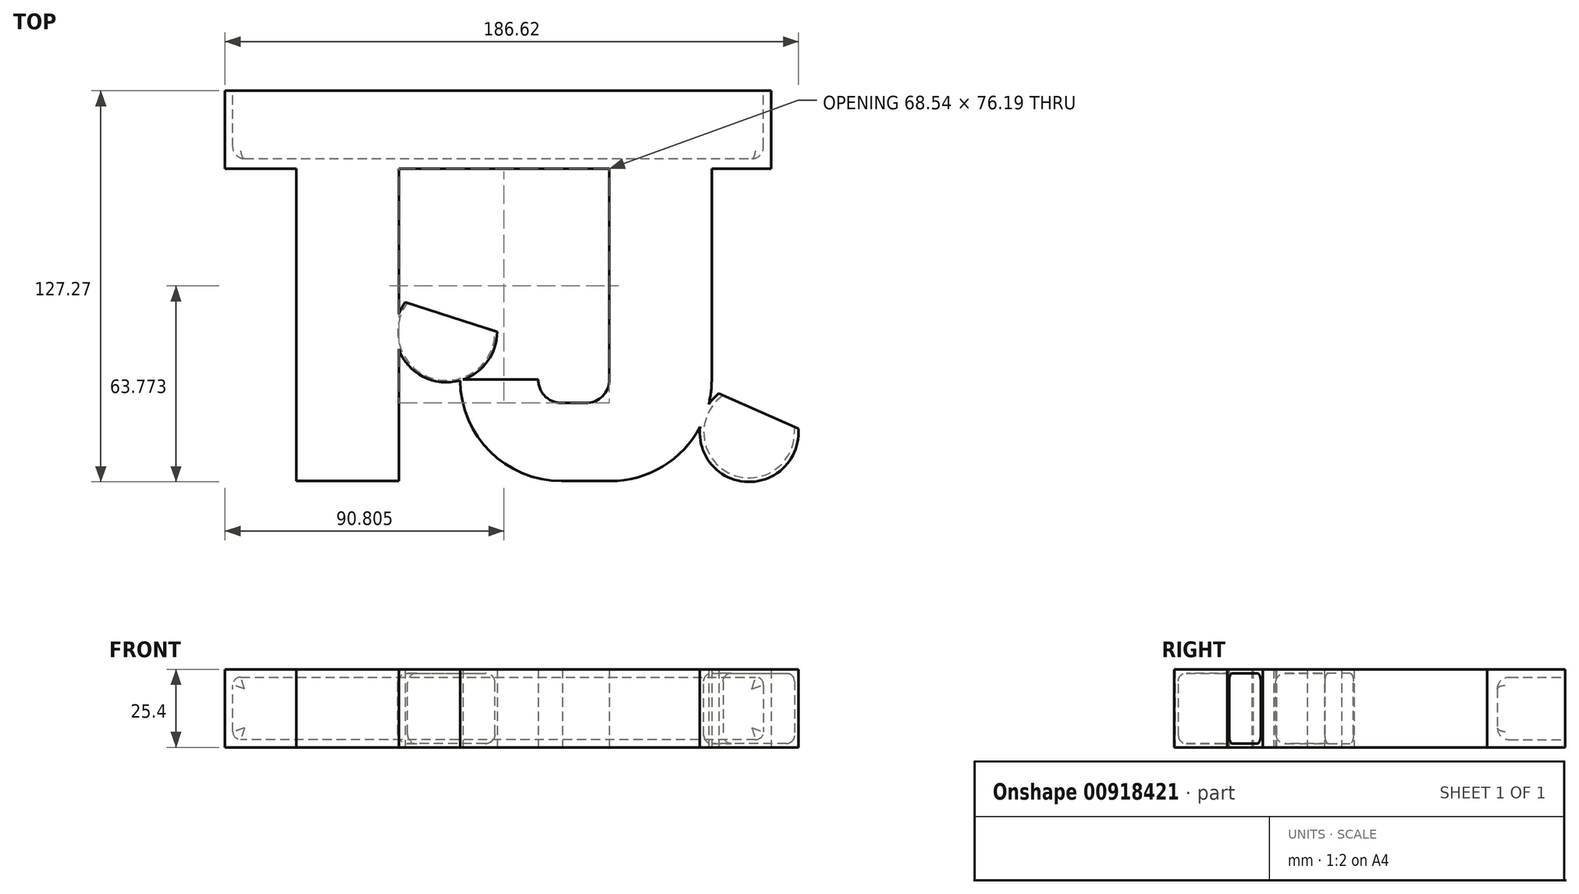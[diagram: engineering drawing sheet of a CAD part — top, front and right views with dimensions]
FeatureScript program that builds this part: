
annotation { "Feature Type Name" : "Feature", "Feature Type Description" : "" }
export const myFeature = defineFeature(function(context is Context, id is Id, definition is map)
    precondition{}
    {
        {
            var Q0;
            Q0=qCreatedBy(makeId("Top.planeOp"),FACE);
            var sketch = newSketch(context, id + "F0", { "sketchPlane" : qUnion([Q0])});
            skLineSegment(sketch, "E0.bottom", {"start": v(88.9, -63.5) * mm, "end": v(-88.9, -63.5) * mm, "construction": true});
            skLineSegment(sketch, "E0.top", {"start": v(88.9, 63.5) * mm, "end": v(-88.9, 63.5) * mm, "construction": true});
            skLineSegment(sketch, "E0.left", {"start": v(88.9, -63.5) * mm, "end": v(88.9, 63.5) * mm, "construction": true});
            skPoint(sketch, "E0.middle", {"position": v(0, 0) * mm});
            skLineSegment(sketch, "E1.bottom", {"start": v(-88.9, 63.5) * mm, "end": v(88.9, 63.5) * mm});
            skLineSegment(sketch, "E1.top", {"start": v(-88.9, 38.1) * mm, "end": v(-65.68, 38.1) * mm});
            skLineSegment(sketch, "E1.left", {"start": v(-88.9, 63.5) * mm, "end": v(-88.9, 38.1) * mm});
            skLineSegment(sketch, "E1.right", {"start": v(88.9, 63.5) * mm, "end": v(88.9, 38.1) * mm});
            skLineSegment(sketch, "E2.left", {"start": v(-65.68, 38.1) * mm, "end": v(-65.68, -63.5) * mm});
            skLineSegment(sketch, "E2.right", {"start": v(-32.37, 38.1) * mm, "end": v(-32.37, -63.5) * mm});
            skPoint(sketch, "E3", {"position": v(0, 63.5) * mm});
            skLineSegment(sketch, "E4", {"start": v(0, 0) * mm, "end": v(0, 72.92) * mm});
            skPoint(sketch, "E5", {"position": v(-88.9, 50.8) * mm});
            skLineSegment(sketch, "E6", {"start": v(-88.9, 50.8) * mm, "end": v(0, 50.8) * mm, "construction": true});
            skPoint(sketch, "E7", {"position": v(-44.45, 50.8) * mm});
            skLineSegment(sketch, "E8", {"start": v(-44.45, 50.8) * mm, "end": v(-44.45, 38.1) * mm, "construction": true});
            skPoint(sketch, "E9", {"position": v(-44.45, 38.1) * mm});
            skLineSegment(sketch, "E10.MirrorCS", {"start": v(36.18, 38.1) * mm, "end": v(36.18, -30.47) * mm});
            skLineSegment(sketch, "E11.MirrorCS", {"start": v(69.49, 38.1) * mm, "end": v(69.49, -30.48) * mm});
            skLineSegment(sketch, "E12.MirrorCS", {"start": v(36.47, -63.5) * mm, "end": v(36.18, -63.5) * mm});
            skLineSegment(sketch, "E13", {"start": v(61.1, -13.5) * mm, "end": v(27.8, -13.5) * mm, "construction": true});
            skPoint(sketch, "E14.visualSharp", {"position": v(61.1, -63.5) * mm});
            skArc(sketch, "E14.filletArc", {"start": v(36.47, -63.5) * mm, "mid": v(59.82, -53.83) * mm, "end": v(69.49, -30.48) * mm});
            skLineSegment(sketch, "E15", {"start": v(27.8, -13.5) * mm, "end": v(-19.57, -13.5) * mm, "construction": true});
            skArc(sketch, "E16", {"start": v(-12.4, -30.48) * mm, "mid": v(-2.73, -53.83) * mm, "end": v(20.62, -63.5) * mm});
            skLineSegment(sketch, "E17", {"start": v(20.62, -63.5) * mm, "end": v(34.92, -63.5) * mm});
            skLineSegment(sketch, "E18", {"start": v(-12.4, -30.48) * mm, "end": v(13, -30.48) * mm});
            skArc(sketch, "E19.0", {"start": v(13, -30.48) * mm, "mid": v(15.34, -35.97) * mm, "end": v(20.91, -38.1) * mm});
            skLineSegment(sketch, "E20", {"start": v(20.91, -38.1) * mm, "end": v(28.56, -38.1) * mm});
            skPoint(sketch, "E21.newPointB", {"position": v(27.8, -63.5) * mm});
            skArc(sketch, "E21.filletArc", {"start": v(28.56, -38.1) * mm, "mid": v(33.95, -35.86) * mm, "end": v(36.18, -30.47) * mm});
            skLineSegment(sketch, "E22", {"start": v(34.92, -63.5) * mm, "end": v(36.18, -63.5) * mm});
            skLineSegment(sketch, "E23", {"start": v(-65.68, -63.5) * mm, "end": v(-32.37, -63.5) * mm});
            skLineSegment(sketch, "E24.trimOffspring", {"start": v(-32.37, 38.1) * mm, "end": v(36.18, 38.1) * mm});
            skLineSegment(sketch, "E25.trimOffspring", {"start": v(69.49, 38.1) * mm, "end": v(88.9, 38.1) * mm});
            skSolve(sketch);
        }
        {
            var Q0;
            Q0=makeQuery(id+"F0.imprint","IMPRINT",FACE,{"disambiguationData":[TD([[makeQuery(id+"F0.imprint","IMPRINT",EDGE,{"derivedFrom":sQuery(id+"F0.wireOp",EDGE,"E1.top")}),1.0]])]});
            var Q1;
            {var subQ0=sQuery(id+"F0.wireOp",EDGE,"E1.right");Q1=makeQuery(id+"F0.imprint","IMPRINT",FACE,{"disambiguationData":[TD([[makeQuery(id+"F0.imprint","IMPRINT",EDGE,{"derivedFrom":subQ0}),-1.0]])]});}
            extrude(context, id + "F1", {"entities" : qUnion([Q0, Q1]), "depth" : 25.4 * mm, "offsetDistance" : 25.4 * mm});
        }
        {
            var Q0;
            Q0=makeQuery(id+"F1.opExtrude","SWEPT_FACE",FACE,{"disambiguationData":[OSD([sQuery(id+"F0.wireOp",EDGE,"E1.bottom")])]});
            var sketch = newSketch(context, id + "F2", { "sketchPlane" : qUnion([Q0])});
            skLineSegment(sketch, "E26.0", {"start": v(-83.82, 2.54) * mm, "end": v(83.82, 2.54) * mm});
            skLineSegment(sketch, "E26.1", {"start": v(-86.36, 20.32) * mm, "end": v(-86.36, 5.08) * mm});
            skLineSegment(sketch, "E26.2", {"start": v(83.82, 22.86) * mm, "end": v(-83.82, 22.86) * mm});
            skLineSegment(sketch, "E26.3", {"start": v(86.36, 5.08) * mm, "end": v(86.36, 20.32) * mm});
            skPoint(sketch, "E27.visualSharp", {"position": v(-86.36, 22.86) * mm});
            skArc(sketch, "E27.filletArc", {"start": v(-83.82, 22.86) * mm, "mid": v(-85.62, 22.12) * mm, "end": v(-86.36, 20.32) * mm});
            skPoint(sketch, "E28.visualSharp", {"position": v(-86.36, 2.54) * mm});
            skArc(sketch, "E28.filletArc", {"start": v(-86.36, 5.08) * mm, "mid": v(-85.62, 3.28) * mm, "end": v(-83.82, 2.54) * mm});
            skPoint(sketch, "E29.visualSharp", {"position": v(86.36, 2.54) * mm});
            skArc(sketch, "E29.filletArc", {"start": v(83.82, 2.54) * mm, "mid": v(85.62, 3.28) * mm, "end": v(86.36, 5.08) * mm});
            skPoint(sketch, "E30.visualSharp", {"position": v(86.36, 22.86) * mm});
            skArc(sketch, "E30.filletArc", {"start": v(86.36, 20.32) * mm, "mid": v(85.62, 22.12) * mm, "end": v(83.82, 22.86) * mm});
            skSolve(sketch);
        }
        {
            var Q0;
            Q0=makeQuery(id+"F2.imprint","IMPRINT",FACE,{"disambiguationData":[TD([[makeQuery(id+"F2.imprint","IMPRINT",EDGE,{"derivedFrom":sQuery(id+"F2.wireOp",EDGE,"E26.0")}),1.0]])]});
            extrude(context, id + "F3", {"entities" : qUnion([Q0]), "operationType" : NewBodyOperationType.REMOVE, "oppositeDirection" : true, "depth" : 22.1 * mm, "offsetDistance" : 25.4 * mm});
        }
        {
            var Q0;
            Q0=makeQuery(id+"F3.boolean.opBoolean","COPY",FACE,{"derivedFrom":makeQuery(id+"F3.opExtrude","CAP_FACE",FACE,{"disambiguationData":[OSD([sQuery(id+"F2.wireOp",EDGE,"E26.0"),sQuery(id+"F2.wireOp",EDGE,"E26.1"),sQuery(id+"F2.wireOp",EDGE,"E26.2"),sQuery(id+"F2.wireOp",EDGE,"E26.3"),sQuery(id+"F2.wireOp",EDGE,"E27.filletArc"),sQuery(id+"F2.wireOp",EDGE,"E28.filletArc"),sQuery(id+"F2.wireOp",EDGE,"E29.filletArc"),sQuery(id+"F2.wireOp",EDGE,"E30.filletArc")])],"isStart":false})});
            fillet(context, id + "F4", {"entities" : qUnion([Q0]), "radius" : 3.8 * mm, "tangentPropagation" : true, "allowEdgeOverflow" : false});
        }
        {
            var Q0;
            Q0=qCreatedBy(makeId("Top.planeOp"),FACE);
            var sketch = newSketch(context, id + "F5", { "sketchPlane" : qUnion([Q0])});
            skLineSegment(sketch, "E31.0", {"start": v(-32.37, 38.1) * mm, "end": v(-32.37, -63.5) * mm});
            skPoint(sketch, "E32.0", {"position": v(-12.4, -30.48) * mm});
            skArc(sketch, "E33", {"start": v(-30.23, -5.23) * mm, "mid": v(-21.95, -30.6) * mm, "end": v(-0.37, -14.9) * mm});
            skPoint(sketch, "E33.first.point", {"position": v(-32.37, -14.9) * mm});
            skPoint(sketch, "E33.third.point", {"position": v(-10.32, 0) * mm});
            skArc(sketch, "E34.0", {"start": v(36.47, -63.5) * mm, "mid": v(59.82, -53.83) * mm, "end": v(69.49, -30.48) * mm});
            skArc(sketch, "E35", {"start": v(71.84, -35) * mm, "mid": v(75.13, -62.38) * mm, "end": v(97.67, -46.5) * mm});
            skLineSegment(sketch, "E36", {"start": v(36.47, -63.5) * mm, "end": v(113.1, -63.95) * mm, "construction": true});
            skLineSegment(sketch, "E37", {"start": v(71.84, -35) * mm, "end": v(97.67, -46.5) * mm});
            skLineSegment(sketch, "E38", {"start": v(-30.23, -5.23) * mm, "end": v(-0.37, -14.9) * mm});
            skSolve(sketch);
        }
        {
            var Q0;
            {var subQ4=sQuery(id+"F5.wireOp",EDGE,"E38");Q0=makeQuery(id+"F5.imprint","IMPRINT",FACE,{"disambiguationData":[TD([[makeQuery(id+"F5.imprint","IMPRINT",EDGE,{"derivedFrom":subQ4}),-1.0]])]});}
            var Q1;
            {var subQ4=sQuery(id+"F5.wireOp",EDGE,"E37");Q1=makeQuery(id+"F5.imprint","IMPRINT",FACE,{"disambiguationData":[TD([[makeQuery(id+"F5.imprint","IMPRINT",EDGE,{"derivedFrom":subQ4}),-1.0]])]});}
            extrude(context, id + "F6", {"entities" : qUnion([Q0, Q1]), "operationType" : NewBodyOperationType.ADD, "depth" : 25.4 * mm, "offsetDistance" : 25.4 * mm});
        }
        {
            var Q0;
            Q0=makeQuery(id+"F1.opExtrude","SWEPT_FACE",FACE,{"disambiguationData":[OSD([sQuery(id+"F0.wireOp",EDGE,"E18")])]});
            cPlane(context, id + "F7", {"entities" : qUnion([Q0]), "cplaneType" : CPlaneType.OFFSET, "offset" : 25.4 * mm, "width" : 152.4 * mm, "height" : 152.4 * mm});
        }
        {
            var Q0;
            Q0=qCreatedBy(id+"F7.planeOp",FACE);
            var sketch = newSketch(context, id + "F8", { "sketchPlane" : qUnion([Q0])});
            skLineSegment(sketch, "E39.0", {"start": v(1.64, 1.27) * mm, "end": v(28.96, 1.27) * mm});
            skLineSegment(sketch, "E39.1", {"start": v(1.64, 24.13) * mm, "end": v(1.64, 1.27) * mm});
            skLineSegment(sketch, "E39.2", {"start": v(28.96, 24.13) * mm, "end": v(1.64, 24.13) * mm});
            skLineSegment(sketch, "E39.3", {"start": v(28.96, 1.27) * mm, "end": v(28.96, 24.13) * mm});
            skSolve(sketch);
        }
        {
            var Q0;
            Q0=makeQuery(id+"F8.imprint","IMPRINT",FACE,{"disambiguationData":[TD([[makeQuery(id+"F8.imprint","IMPRINT",EDGE,{"derivedFrom":sQuery(id+"F8.wireOp",EDGE,"E39.0")}),1.0]])]});
            extrude(context, id + "F9", {"entities" : qUnion([Q0]), "operationType" : NewBodyOperationType.REMOVE, "oppositeDirection" : true, "depth" : 14.15 * mm, "offsetDistance" : 25.4 * mm});
        }
        {
            var Q0;
            Q0=makeQuery(id+"F9.boolean.opBoolean","COPY",FACE,{"derivedFrom":makeQuery(id+"F9.opExtrude","CAP_FACE",FACE,{"disambiguationData":[OSD([sQuery(id+"F8.wireOp",EDGE,"E39.0"),sQuery(id+"F8.wireOp",EDGE,"E39.1"),sQuery(id+"F8.wireOp",EDGE,"E39.2"),sQuery(id+"F8.wireOp",EDGE,"E39.3")])],"isStart":false})});
            var sketch = newSketch(context, id + "F10", { "sketchPlane" : qUnion([Q0])});
            skLineSegment(sketch, "E40.bottom", {"start": v(19.77, 1.27) * mm, "end": v(1.64, 1.27) * mm});
            skLineSegment(sketch, "E40.top", {"start": v(19.77, 24.13) * mm, "end": v(1.64, 24.13) * mm});
            skLineSegment(sketch, "E40.left", {"start": v(19.77, 1.27) * mm, "end": v(19.77, 24.13) * mm});
            skLineSegment(sketch, "E40.right", {"start": v(1.64, 1.27) * mm, "end": v(1.64, 24.13) * mm});
            skPoint(sketch, "E41.0", {"position": v(16.87, 0) * mm});
            skLineSegment(sketch, "E42", {"start": v(16.87, 0) * mm, "end": v(16.87, 24.13) * mm});
            skSolve(sketch);
        }
        {
            var Q0;
            Q0=qCreatedBy(id+"F7.planeOp",FACE);
            cPlane(context, id + "F11", {"entities" : qUnion([Q0]), "cplaneType" : CPlaneType.OFFSET, "offset" : 9.83 * mm, "oppositeDirection" : true, "width" : 152.4 * mm, "height" : 152.4 * mm});
        }
        {
            var Q0;
            Q0=qCreatedBy(id+"F11.planeOp",FACE);
            var sketch = newSketch(context, id + "F12", { "sketchPlane" : qUnion([Q0])});
            skPoint(sketch, "E43.0", {"position": v(16.87, 0) * mm});
            skLineSegment(sketch, "E44", {"start": v(16.87, 0) * mm, "end": v(16.87, 13.06) * mm});
            skSolve(sketch);
        }
        {
            var Q0;
            {var subQ0=sQuery(id+"F10.wireOp",EDGE,"E40.right");Q0=makeQuery(id+"F10.imprint","IMPRINT",FACE,{"disambiguationData":[TD([[makeQuery(id+"F10.imprint","IMPRINT",EDGE,{"derivedFrom":subQ0}),1.0]])]});}
            var Q1;
            Q1=sQuery(id+"F12.wireOp",EDGE,"E44");
            revolve(context, id + "F13", {"operationType" : NewBodyOperationType.REMOVE, "surfaceOperationType" : NewSurfaceOperationType.NEW, "entities" : qUnion([Q0]), "axis" : qUnion([Q1]), "revolveType" : RevolveType.FULL, "oppositeDirection" : true});
        }
        {
            var Q0;
            Q0=qCreatedBy(id+"F11.planeOp",FACE);
            var sketch = newSketch(context, id + "F14", { "sketchPlane" : qUnion([Q0])});
            skLineSegment(sketch, "E45.0", {"start": v(-96.4, 1.27) * mm, "end": v(-73.1, 1.27) * mm});
            skLineSegment(sketch, "E45.1", {"start": v(-96.4, 24.13) * mm, "end": v(-96.4, 1.27) * mm});
            skLineSegment(sketch, "E45.2", {"start": v(-73.1, 24.13) * mm, "end": v(-96.4, 24.13) * mm});
            skLineSegment(sketch, "E45.3", {"start": v(-73.1, 1.27) * mm, "end": v(-73.1, 24.13) * mm});
            skSolve(sketch);
        }
        {
            var Q0;
            Q0=makeQuery(id+"F14.imprint","IMPRINT",FACE,{"disambiguationData":[TD([[makeQuery(id+"F14.imprint","IMPRINT",EDGE,{"derivedFrom":sQuery(id+"F14.wireOp",EDGE,"E45.0")}),1.0]])]});
            extrude(context, id + "F15", {"entities" : qUnion([Q0]), "operationType" : NewBodyOperationType.REMOVE, "oppositeDirection" : true, "depth" : 32.8 * mm, "offsetDistance" : 25.4 * mm});
        }
        {
            var Q0;
            Q0=makeQuery(id+"F15.boolean.opBoolean","COPY",FACE,{"derivedFrom":makeQuery(id+"F15.opExtrude","CAP_FACE",FACE,{"disambiguationData":[OSD([sQuery(id+"F14.wireOp",EDGE,"E45.0"),sQuery(id+"F14.wireOp",EDGE,"E45.1"),sQuery(id+"F14.wireOp",EDGE,"E45.2"),sQuery(id+"F14.wireOp",EDGE,"E45.3")])],"isStart":false})});
            var sketch = newSketch(context, id + "F16", { "sketchPlane" : qUnion([Q0])});
            skPoint(sketch, "E46.0", {"position": v(-81.66, 0) * mm});
            skLineSegment(sketch, "E47", {"start": v(-81.66, 0) * mm, "end": v(-81.66, 24.13) * mm});
            skLineSegment(sketch, "E48.bottom", {"start": v(-81.66, 1.27) * mm, "end": v(-96.4, 1.27) * mm});
            skLineSegment(sketch, "E48.top", {"start": v(-81.66, 24.13) * mm, "end": v(-96.4, 24.13) * mm});
            skLineSegment(sketch, "E48.left", {"start": v(-81.66, 1.27) * mm, "end": v(-81.66, 24.13) * mm});
            skLineSegment(sketch, "E48.right", {"start": v(-96.4, 1.27) * mm, "end": v(-96.4, 24.13) * mm});
            skSolve(sketch);
        }
        {
            var Q0;
            Q0=makeQuery(id+"F16.imprint","IMPRINT",FACE,{"disambiguationData":[TD([[makeQuery(id+"F16.imprint","IMPRINT",EDGE,{"derivedFrom":sQuery(id+"F16.wireOp",EDGE,"E48.bottom")}),1.0]])]});
            var Q1;
            Q1=sQuery(id+"F16.wireOp",EDGE,"E47");
            revolve(context, id + "F17", {"operationType" : NewBodyOperationType.REMOVE, "surfaceOperationType" : NewSurfaceOperationType.NEW, "entities" : qUnion([Q0]), "axis" : qUnion([Q1]), "revolveType" : RevolveType.FULL, "oppositeDirection" : true});
        }
        {
            var Q0;
            Q0=makeQuery(id+"F13.boolean.opBoolean","COPY",EDGE,{"derivedFrom":makeQuery(id+"F13.opRevolve","SWEPT_EDGE",EDGE,{"disambiguationData":[OSD([sQuery(id+"F10.wireOp",EDGE,"E40.bottom"),sQuery(id+"F10.wireOp",EDGE,"E40.right")])]})});
            var Q1;
            Q1=makeQuery(id+"F13.boolean.opBoolean","COPY",EDGE,{"derivedFrom":makeQuery(id+"F13.opRevolve","SWEPT_EDGE",EDGE,{"disambiguationData":[OSD([sQuery(id+"F10.wireOp",EDGE,"E40.top"),sQuery(id+"F10.wireOp",EDGE,"E40.right")])]})});
            fillet(context, id + "F18", {"entities" : qUnion([Q0, Q1]), "radius" : 3.07 * mm, "tangentPropagation" : true, "allowEdgeOverflow" : false});
        }
        {
            var Q0;
            Q0=makeQuery(id+"F17.boolean.opBoolean","MERGE",FACE,{"derivedFrom":[makeQuery(id+"F15.boolean.opBoolean","COPY",FACE,{"derivedFrom":makeQuery(id+"F15.opExtrude","SWEPT_FACE",FACE,{"disambiguationData":[OSD([sQuery(id+"F14.wireOp",EDGE,"E45.0")])]})})],"fromTools":[makeQuery(id+"F17.opRevolve","SWEPT_FACE",FACE,{"disambiguationData":[OSD([sQuery(id+"F16.wireOp",EDGE,"E48.bottom")])]})]});
            var sketch = newSketch(context, id + "F19", { "sketchPlane" : qUnion([Q0])});
            skLineSegment(sketch, "E49", {"start": v(73.1, -35.69) * mm, "end": v(73.21, -35.62) * mm});
            skLineSegment(sketch, "E50", {"start": v(73.21, -35.62) * mm, "end": v(73.1, -35.57) * mm});
            skLineSegment(sketch, "E51", {"start": v(73.1, -35.57) * mm, "end": v(73.1, -35.69) * mm});
            skSolve(sketch);
        }
        {
            var Q0;
            Q0=makeQuery(id+"F19.imprint","IMPRINT",FACE,{"disambiguationData":[TD([[makeQuery(id+"F19.imprint","IMPRINT",EDGE,{"derivedFrom":sQuery(id+"F19.wireOp",EDGE,"E49")}),1.0]])]});
            extrude(context, id + "F20", {"entities" : qUnion([Q0]), "operationType" : NewBodyOperationType.ADD, "depth" : 23.27 * mm, "offsetDistance" : 25.4 * mm});
        }
        {
            var Q0;
            Q0=makeQuery(id+"F17.boolean.opBoolean","COPY",EDGE,{"derivedFrom":makeQuery(id+"F17.opRevolve","SWEPT_EDGE",EDGE,{"disambiguationData":[OSD([sQuery(id+"F16.wireOp",EDGE,"E48.bottom"),sQuery(id+"F16.wireOp",EDGE,"E48.right")])]})});
            var Q1;
            Q1=makeQuery(id+"F17.boolean.opBoolean","COPY",EDGE,{"derivedFrom":makeQuery(id+"F17.opRevolve","SWEPT_EDGE",EDGE,{"disambiguationData":[OSD([sQuery(id+"F16.wireOp",EDGE,"E48.top"),sQuery(id+"F16.wireOp",EDGE,"E48.right")])]})});
            fillet(context, id + "F21", {"entities" : qUnion([Q0, Q1]), "radius" : 2.54 * mm, "tangentPropagation" : true, "allowEdgeOverflow" : false});
        }
    });
